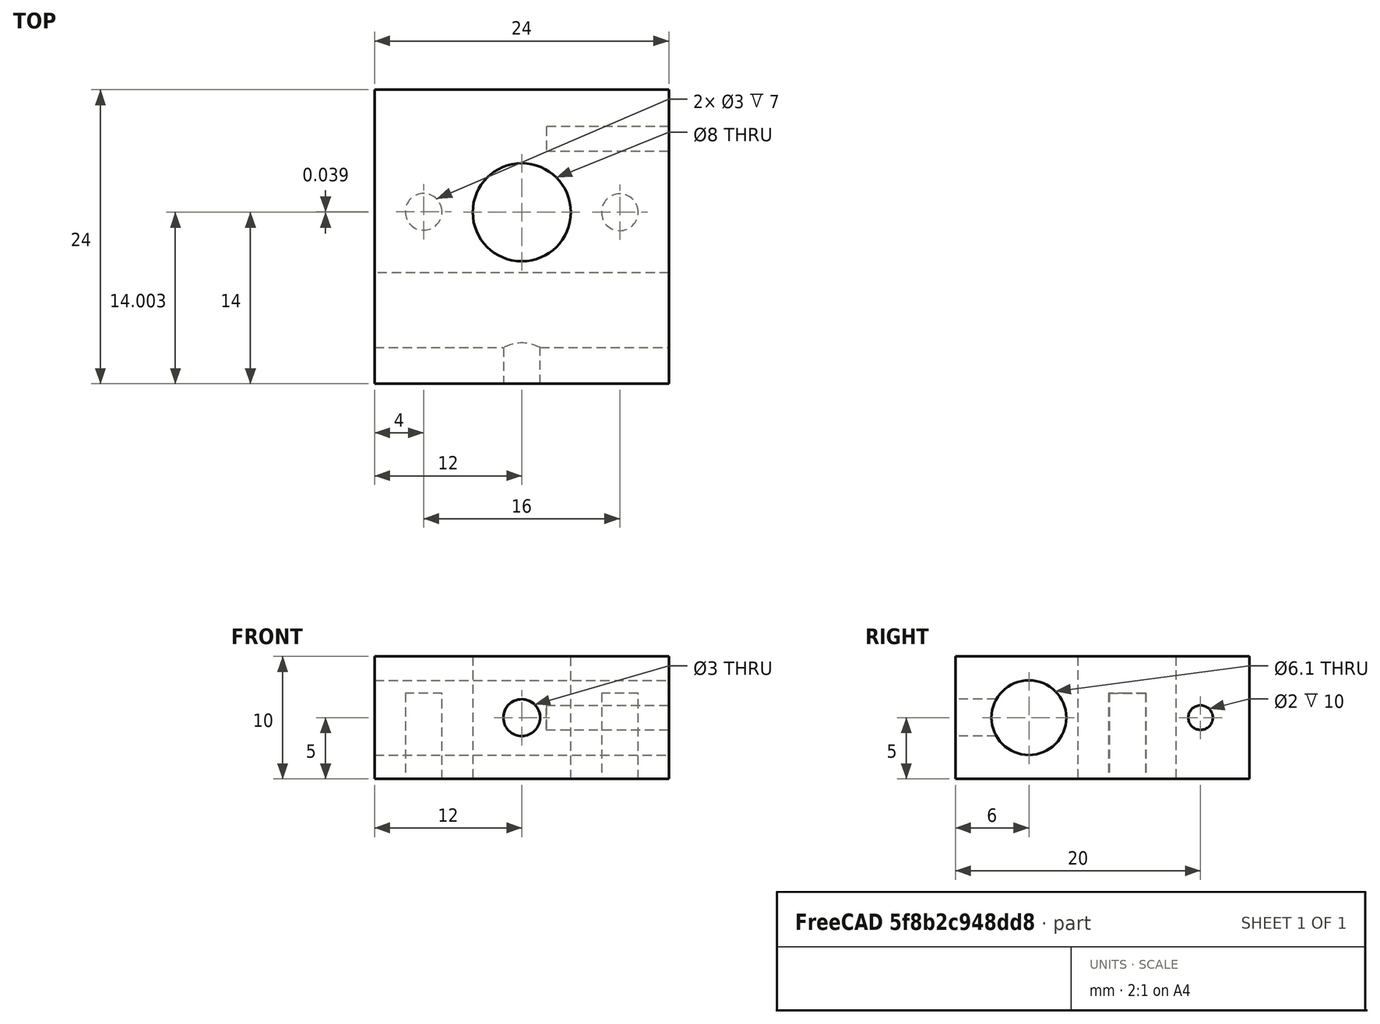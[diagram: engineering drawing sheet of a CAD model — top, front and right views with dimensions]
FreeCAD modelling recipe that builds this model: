
FCSTD DOCUMENT  (FreeCAD 0.19R24291 (Git))
Label: FilPullHB_v1с
License: All rights reserved
LicenseURL: http://en.wikipedia.org/wiki/All_rights_reserved
objects: TechDraw::DrawViewDimension×19, Sketcher::SketchObject×5, TechDraw::DrawViewBalloon×5, PartDesign::Pocket×4, TechDraw::DrawViewPart×4, PartDesign::Pad×1, TechDraw::DrawSVGTemplate×1, PartDesign::Body×1, TechDraw::DrawPage×1
note: 16 computed .brp shape members not serialized (recipe doc carries the construction recipe); baked Part::Feature solids carry a one-line shape summary decoded from their .brp

FEATURE [Sketcher::SketchObject] Sketch
  FullyConstrained = true
  MapMode = 5
  Support = -> [XY_Plane]
  expr: Constraints[9] = 8 / 2
  sketch-geometry (5):
    g0: LineSegment StartX=-12 StartY=10 StartZ=0 EndX=12 EndY=10 EndZ=0
    g1: LineSegment StartX=12 StartY=10 StartZ=0 EndX=12 EndY=-14 EndZ=0
    g2: LineSegment StartX=12 StartY=-14 StartZ=0 EndX=-12 EndY=-14 EndZ=0
    g3: LineSegment StartX=-12 StartY=-14 StartZ=0 EndX=-12 EndY=10 EndZ=0
    g4: Circle CenterX=0 CenterY=0 CenterZ=0 NormalX=0 NormalY=0 NormalZ=1 AngleXU=0 Radius=4
  constraints (13):
    c: Coincident(g0,g1)
    c: Coincident(g1,g2)
    c: Coincident(g2,g3)
    c: Coincident(g3,g0)
    c: Horizontal(g2)
    c: Vertical(g1)
    c: Vertical(g3)
    c: Symmetric(g0,g0,g-2)
    c: Coincident(g4,g-1)
    c: Radius(g4) = 4
    c: Distance(g0) = 24
    c: Distance(g4,g0) = 10
    c: Distance(g4,g2) = 14
FEATURE [PartDesign::Pad] Pad
  Direction = (1,1,1)
  Length = 10
  Length2 = 100
  Profile = -> Sketch
  Type = 0
FEATURE [Sketcher::SketchObject] Sketch002
  FullyConstrained = true
  MapMode = 5
  Placement = pos=(12,0,0) rot=(0.57735,0.57735,0.57735;2.0944rad)
  sketch-geometry (1):
    g0: Circle CenterX=-8 CenterY=5 CenterZ=0 NormalX=0 NormalY=0 NormalZ=1 AngleXU=0 Radius=3.05
  constraints (3):
    c: DistanceY(g-1,g0) = 5
    c: Radius(g0) = 3.05
    c: DistanceX(g-2,g0) = -8
FEATURE [PartDesign::Pocket] Pocket
  BaseFeature = -> Pad
  Length = 5
  Length2 = 100
  Profile = -> Sketch002
  Type = 1
FEATURE [Sketcher::SketchObject] Sketch003
  FullyConstrained = true
  MapMode = 5
  Placement = pos=(12,0,0) rot=(0.57735,0.57735,0.57735;2.0944rad)
  Support = -> [Pocket]
  sketch-geometry (1):
    g0: Circle CenterX=6 CenterY=5 CenterZ=0 NormalX=0 NormalY=0 NormalZ=1 AngleXU=0 Radius=1
  constraints (3):
    c: DistanceY(g-1,g0) = 5
    c: DistanceX(g-2,g0) = 6
    c: Radius(g0) = 1
FEATURE [PartDesign::Pocket] Pocket001
  BaseFeature = -> Pocket
  Length = 10
  Length2 = 100
  Profile = -> Sketch003
  Type = 0
FEATURE [Sketcher::SketchObject] Sketch004
  FullyConstrained = false
  MapMode = 5
  Placement = pos=(0,0,0) rot=(1,0,0;3.14159rad)
  Support = -> [Pocket001]
  sketch-geometry (2):
    g0: Circle CenterX=8 CenterY=-0.003153 CenterZ=0 NormalX=0 NormalY=0 NormalZ=1 AngleXU=0 Radius=1.5
    g1: Circle CenterX=-8 CenterY=-0.04227 CenterZ=0 NormalX=0 NormalY=0 NormalZ=1 AngleXU=0 Radius=1.5
  constraints (4):
    c: Radius(g0) = 1.5
    c: Radius(g1) = 1.5
    c: DistanceX(g-2,g1) = -8
    c: DistanceX(g-2,g0) = 8
FEATURE [PartDesign::Pocket] Pocket002
  BaseFeature = -> Pocket001
  Length = 7
  Length2 = 100
  Profile = -> Sketch004
  Type = 0
FEATURE [Sketcher::SketchObject] Sketch005
  FullyConstrained = true
  MapMode = 5
  Placement = pos=(0,-14,0) rot=(1,0,0;1.5708rad)
  Support = -> [Pocket002]
  sketch-geometry (1):
    g0: Circle CenterX=0 CenterY=5 CenterZ=0 NormalX=0 NormalY=0 NormalZ=1 AngleXU=0 Radius=1.5
  constraints (3):
    c: PointOnObject(g0,g-2)
    c: DistanceY(g-1,g0) = 5
    c: Radius(g0) = 1.5
FEATURE [TechDraw::DrawSVGTemplate] Template
  Height = 210
  Orientation = 1
  Width = 297
FEATURE [PartDesign::Pocket] Pocket003
  BaseFeature = -> Pocket002
  Length = 5
  Length2 = 100
  Profile = -> Sketch005
  Type = 0
FEATURE [PartDesign::Body] Body
  Group = -> [Sketch,Pad,Sketch002,Pocket,Sketch003,Pocket001,Sketch004,Pocket002,Sketch005,Pocket003]
  Origin = -> Origin
  Tip = -> Pocket003
FEATURE [TechDraw::DrawViewPart] View
  CoarseView = false
  Direction = (-0.484,-0.723,-0.493)
  Focus = 100
  HardHidden = false
  IsoCount = 0
  IsoHidden = false
  IsoVisible = false
  LockPosition = false
  Perspective = false
  Rotation = 0
  Scale = 3
  ScaleType = 0
  SeamHidden = false
  SeamVisible = true
  SmoothHidden = false
  SmoothVisible = true
  Source = -> [Pocket003]
  X = 102.429
  XDirection = (-0.8,0.593,-0.085)
  Y = 63.845
FEATURE [TechDraw::DrawViewPart] View001  label="Top"
  Caption = Top
  CoarseView = false
  Direction = (0,0,-1)
  Focus = 100
  HardHidden = false
  IsoCount = 0
  IsoHidden = false
  IsoVisible = false
  LockPosition = false
  Perspective = false
  Rotation = 0
  Scale = 3
  ScaleType = 0
  SeamHidden = false
  SeamVisible = true
  SmoothHidden = false
  SmoothVisible = true
  Source = -> [Pocket003]
  X = 205.686
  XDirection = (-1,0,0)
  Y = 155.514
FEATURE [TechDraw::DrawViewPart] View002  label="Left"
  Caption = Left
  CoarseView = false
  Direction = (1,0,0)
  Focus = 100
  HardHidden = false
  IsoCount = 0
  IsoHidden = false
  IsoVisible = false
  LockPosition = false
  Perspective = false
  Rotation = 0
  Scale = 3
  ScaleType = 0
  SeamHidden = false
  SeamVisible = true
  SmoothHidden = false
  SmoothVisible = true
  Source = -> [Pocket003]
  X = 116.412
  XDirection = (0,0,-1)
  Y = 156.785
FEATURE [TechDraw::DrawViewPart] View003  label="Front"
  Caption = Front
  CoarseView = false
  Direction = (0,-1,0)
  Focus = 100
  HardHidden = false
  IsoCount = 0
  IsoHidden = false
  IsoVisible = false
  LockPosition = false
  Perspective = false
  Rotation = 0
  Scale = 3
  ScaleType = 0
  SeamHidden = false
  SeamVisible = true
  SmoothHidden = false
  SmoothVisible = true
  Source = -> [Pocket003]
  X = 208.228
  XDirection = (-1,0,0)
  Y = 62.4281
FEATURE [TechDraw::DrawViewDimension] Dimension
  Arbitrary = false
  ArbitraryTolerances = false
  EqualTolerance = true
  FormatSpec = %.2f
  FormatSpecOverTolerance = %+.2f
  FormatSpecUnderTolerance = %+.2f
  Inverted = false
  LockPosition = false
  MeasureType = 1
  OverTolerance = 0
  References2D = -> [View001]
  Rotation = 0
  ScaleType = 0
  TheoreticalExact = false
  Type = 2
  UnderTolerance = 0
  X = 45.1878
  Y = -1.25288
FEATURE [TechDraw::DrawViewDimension] Dimension001
  Arbitrary = false
  ArbitraryTolerances = false
  EqualTolerance = true
  FormatSpec = %.2f
  FormatSpecOverTolerance = %+.2f
  FormatSpecUnderTolerance = %+.2f
  Inverted = false
  LockPosition = false
  MeasureType = 1
  OverTolerance = 0
  References2D = -> [View001]
  Rotation = 0
  ScaleType = 0
  TheoreticalExact = false
  Type = 1
  UnderTolerance = 0
  X = 0.835256
  Y = 48.9465
FEATURE [TechDraw::DrawViewDimension] Dimension002
  Arbitrary = false
  ArbitraryTolerances = false
  EqualTolerance = true
  FormatSpec = ⌀%.2f
  FormatSpecOverTolerance = %+.2f
  FormatSpecUnderTolerance = %+.2f
  Inverted = false
  LockPosition = false
  MeasureType = 1
  OverTolerance = 0
  References2D = -> [View001]
  Rotation = 0
  ScaleType = 0
  TheoreticalExact = false
  Type = 5
  UnderTolerance = 0
  X = 10.8583
  Y = 26.7282
FEATURE [TechDraw::DrawViewDimension] Dimension003
  Arbitrary = false
  ArbitraryTolerances = false
  EqualTolerance = true
  FormatSpec = ⌀%.2f
  FormatSpecOverTolerance = %+.2f
  FormatSpecUnderTolerance = %+.2f
  Inverted = false
  LockPosition = false
  MeasureType = 1
  OverTolerance = 0
  References2D = -> [View001]
  Rotation = 0
  ScaleType = 0
  TheoreticalExact = false
  Type = 5
  UnderTolerance = 0
  X = -18.3756
  Y = 23.8048
FEATURE [TechDraw::DrawViewDimension] Dimension004
  Arbitrary = false
  ArbitraryTolerances = false
  EqualTolerance = true
  FormatSpec = ⌀%.2f
  FormatSpecOverTolerance = %+.2f
  FormatSpecUnderTolerance = %+.2f
  Inverted = false
  LockPosition = false
  MeasureType = 1
  OverTolerance = 0
  References2D = -> [View001]
  Rotation = 0
  ScaleType = 0
  TheoreticalExact = false
  Type = 5
  UnderTolerance = 0
  X = 27.5635
  Y = 20.8814
FEATURE [TechDraw::DrawViewDimension] Dimension005
  Arbitrary = false
  ArbitraryTolerances = false
  EqualTolerance = true
  FormatSpec = %.2f
  FormatSpecOverTolerance = %+.2f
  FormatSpecUnderTolerance = %+.2f
  Inverted = false
  LockPosition = false
  MeasureType = 1
  OverTolerance = 0
  References2D = -> [View001]
  Rotation = 0
  ScaleType = 0
  TheoreticalExact = false
  Type = 1
  UnderTolerance = 0
  X = 8.70097
  Y = -13.0841
FEATURE [TechDraw::DrawViewDimension] Dimension006
  Arbitrary = false
  ArbitraryTolerances = false
  EqualTolerance = true
  FormatSpec = %.2f
  FormatSpecOverTolerance = %+.2f
  FormatSpecUnderTolerance = %+.2f
  Inverted = false
  LockPosition = false
  MeasureType = 1
  OverTolerance = 0
  References2D = -> [View001]
  Rotation = 0
  ScaleType = 0
  TheoreticalExact = false
  Type = 1
  UnderTolerance = 0
  X = -6.1952
  Y = -19.8835
FEATURE [TechDraw::DrawViewDimension] Dimension007
  Arbitrary = false
  ArbitraryTolerances = false
  EqualTolerance = true
  FormatSpec = %.2f
  FormatSpecOverTolerance = %+.2f
  FormatSpecUnderTolerance = %+.2f
  Inverted = false
  LockPosition = false
  MeasureType = 1
  OverTolerance = 0
  References2D = -> [View001]
  Rotation = 0
  ScaleType = 0
  TheoreticalExact = false
  Type = 2
  UnderTolerance = 0
  X = -48.2224
  Y = 24.3458
FEATURE [TechDraw::DrawViewDimension] Dimension008
  Arbitrary = false
  ArbitraryTolerances = false
  EqualTolerance = true
  FormatSpec = %.2f
  FormatSpecOverTolerance = %+.2f
  FormatSpecUnderTolerance = %+.2f
  Inverted = false
  LockPosition = false
  MeasureType = 1
  OverTolerance = 0
  References2D = -> [View003]
  Rotation = 0
  ScaleType = 0
  TheoreticalExact = false
  Type = 2
  UnderTolerance = 0
  X = 40.0923
  Y = -27.9638
FEATURE [TechDraw::DrawViewDimension] Dimension009
  Arbitrary = false
  ArbitraryTolerances = false
  EqualTolerance = true
  FormatSpec = %.2f
  FormatSpecOverTolerance = %+.2f
  FormatSpecUnderTolerance = %+.2f
  Inverted = false
  LockPosition = false
  MeasureType = 1
  OverTolerance = 0
  References2D = -> [View003]
  Rotation = 0
  ScaleType = 0
  TheoreticalExact = false
  Type = 2
  UnderTolerance = 0
  X = 51.0346
  Y = 0.417628
FEATURE [TechDraw::DrawViewDimension] Dimension010
  Arbitrary = false
  ArbitraryTolerances = false
  EqualTolerance = true
  FormatSpec = %.2f
  FormatSpecOverTolerance = %+.2f
  FormatSpecUnderTolerance = %+.2f
  Inverted = false
  LockPosition = false
  MeasureType = 1
  OverTolerance = 0
  References2D = -> [View002]
  Rotation = 0
  ScaleType = 0
  TheoreticalExact = false
  Type = 1
  UnderTolerance = 0
  X = 5.82949
  Y = 5.8048
FEATURE [TechDraw::DrawViewDimension] Dimension011
  Arbitrary = false
  ArbitraryTolerances = false
  EqualTolerance = true
  FormatSpec = %.2f
  FormatSpecOverTolerance = %+.2f
  FormatSpecUnderTolerance = %+.2f
  Inverted = false
  LockPosition = false
  MeasureType = 1
  OverTolerance = 0
  References2D = -> [View002]
  Rotation = 0
  ScaleType = 0
  TheoreticalExact = false
  Type = 1
  UnderTolerance = 0
  X = 7.5
  Y = 18.1532
FEATURE [TechDraw::DrawViewDimension] Dimension012
  Arbitrary = false
  ArbitraryTolerances = false
  EqualTolerance = true
  FormatSpec = ⌀%.2f
  FormatSpecOverTolerance = %+.2f
  FormatSpecUnderTolerance = %+.2f
  Inverted = false
  LockPosition = false
  MeasureType = 1
  OverTolerance = 0
  References2D = -> [View002]
  Rotation = 0
  ScaleType = 0
  TheoreticalExact = false
  Type = 5
  UnderTolerance = 0
  X = 21.299
  Y = 44.6862
FEATURE [TechDraw::DrawViewDimension] Dimension013
  Arbitrary = false
  ArbitraryTolerances = false
  EqualTolerance = true
  FormatSpec = ⌀%.2f
  FormatSpecOverTolerance = %+.2f
  FormatSpecUnderTolerance = %+.2f
  Inverted = false
  LockPosition = false
  MeasureType = 1
  OverTolerance = 0
  References2D = -> [View002]
  Rotation = 0
  ScaleType = 0
  TheoreticalExact = false
  Type = 5
  UnderTolerance = 0
  X = 27.9811
  Y = -3.75865
FEATURE [TechDraw::DrawViewDimension] Dimension014
  Arbitrary = false
  ArbitraryTolerances = false
  EqualTolerance = true
  FormatSpec = %.2f
  FormatSpecOverTolerance = %+.2f
  FormatSpecUnderTolerance = %+.2f
  Inverted = false
  LockPosition = false
  MeasureType = 1
  OverTolerance = 0
  References2D = -> [View002]
  Rotation = 0
  ScaleType = 0
  TheoreticalExact = false
  Type = 2
  UnderTolerance = 0
  X = -39.6747
  Y = 16.6359
FEATURE [TechDraw::DrawViewDimension] Dimension015
  Arbitrary = false
  ArbitraryTolerances = false
  EqualTolerance = true
  FormatSpec = %.2f
  FormatSpecOverTolerance = %+.2f
  FormatSpecUnderTolerance = %+.2f
  Inverted = false
  LockPosition = false
  MeasureType = 1
  OverTolerance = 0
  References2D = -> [View002]
  Rotation = 0
  ScaleType = 0
  TheoreticalExact = false
  Type = 2
  UnderTolerance = 0
  X = -41.3452
  Y = -27.4176
FEATURE [TechDraw::DrawViewBalloon] Balloon
  BubbleShape = 0
  EndType = 0
  EndTypeScale = 1
  KinkLength = 5
  LockPosition = false
  OriginX = 9.32078
  OriginY = 1.91304
  Rotation = 0
  ScaleType = 0
  ShapeScale = 1
  SourceView = -> View001
  Text = M3x5
  TextWrapLen = -1
  X = 20.5814
  Y = 4.26421
FEATURE [TechDraw::DrawViewBalloon] Balloon001
  BubbleShape = 0
  EndType = 0
  EndTypeScale = 1
  KinkLength = 5
  LockPosition = false
  OriginX = 1.09548
  OriginY = 0.22758
  Rotation = 0
  ScaleType = 0
  ShapeScale = 1
  SourceView = -> View003
  Text = M3
  TextWrapLen = -1
  X = 14.4442
  Y = 10.9313
FEATURE [TechDraw::DrawViewBalloon] Balloon002
  BubbleShape = 0
  EndType = 0
  EndTypeScale = 1
  KinkLength = 5
  LockPosition = false
  OriginX = -9.05486
  OriginY = 3.16592
  Rotation = 0
  ScaleType = 0
  ShapeScale = 1
  SourceView = -> View001
  Text = M3x5
  TextWrapLen = -1
  X = -17.1444
  Y = -5.20202
FEATURE [TechDraw::DrawViewBalloon] Balloon003
  BubbleShape = 0
  EndType = 0
  EndTypeScale = 1
  KinkLength = 5
  LockPosition = false
  OriginX = 3.7524
  OriginY = 2.74829
  Rotation = 0
  ScaleType = 0
  ShapeScale = 1
  SourceView = -> View001
  Text = M8
  TextWrapLen = -1
  X = 18.9108
  Y = 15.1225
FEATURE [TechDraw::DrawViewBalloon] Balloon004
  BubbleShape = 0
  EndType = 0
  EndTypeScale = 1
  KinkLength = 5
  LockPosition = false
  OriginX = -0.178319
  OriginY = 8.72832
  Rotation = 0
  ScaleType = 0
  ShapeScale = 1
  SourceView = -> View002
  Text = deep 5mm
  TextWrapLen = -1
  X = -20.9359
  Y = 10.3835
FEATURE [TechDraw::DrawViewDimension] Dimension016
  Arbitrary = false
  ArbitraryTolerances = false
  EqualTolerance = true
  FormatSpec = ⌀%.2f
  FormatSpecOverTolerance = %+.2f
  FormatSpecUnderTolerance = %+.2f
  Inverted = false
  LockPosition = false
  MeasureType = 1
  OverTolerance = 0
  References2D = -> [View003]
  Rotation = 0
  ScaleType = 0
  TheoreticalExact = false
  Type = 5
  UnderTolerance = 0
  X = -14.1994
  Y = 12.9465
FEATURE [TechDraw::DrawViewDimension] Dimension017
  Arbitrary = false
  ArbitraryTolerances = false
  EqualTolerance = true
  FormatSpec = %.2f
  FormatSpecOverTolerance = %+.2f
  FormatSpecUnderTolerance = %+.2f
  Inverted = false
  LockPosition = false
  MeasureType = 1
  OverTolerance = 0
  References2D = -> [View001]
  Rotation = 0
  ScaleType = 0
  TheoreticalExact = false
  Type = 1
  UnderTolerance = 0
  X = -13.4061
  Y = 34.3987
FEATURE [TechDraw::DrawViewDimension] Dimension018
  Arbitrary = false
  ArbitraryTolerances = false
  EqualTolerance = true
  FormatSpec = %.2f
  FormatSpecOverTolerance = %+.2f
  FormatSpecUnderTolerance = %+.2f
  Inverted = false
  LockPosition = false
  MeasureType = 1
  OverTolerance = 0
  References2D = -> [View003]
  Rotation = 0
  ScaleType = 0
  TheoreticalExact = false
  Type = 1
  UnderTolerance = 0
  X = -17.5824
  Y = -2.50577
FEATURE [TechDraw::DrawPage] Page
  KeepUpdated = true
  NextBalloonIndex = 7
  ProjectionType = 0
  Template = -> Template
  Views = -> [View,View001,View002,View003,Dimension,Dimension001,Dimension002,Dimension003,Dimension004,Dimension005,Dimension006,Dimension007,Dimension008,Dimension009,Dimension010,Dimension011,Dimension012,Dimension013,Dimension014,Dimension015,Balloon,Balloon001,Balloon002,Balloon003,Balloon004,Dimension016,Dimension017,Dimension018]
